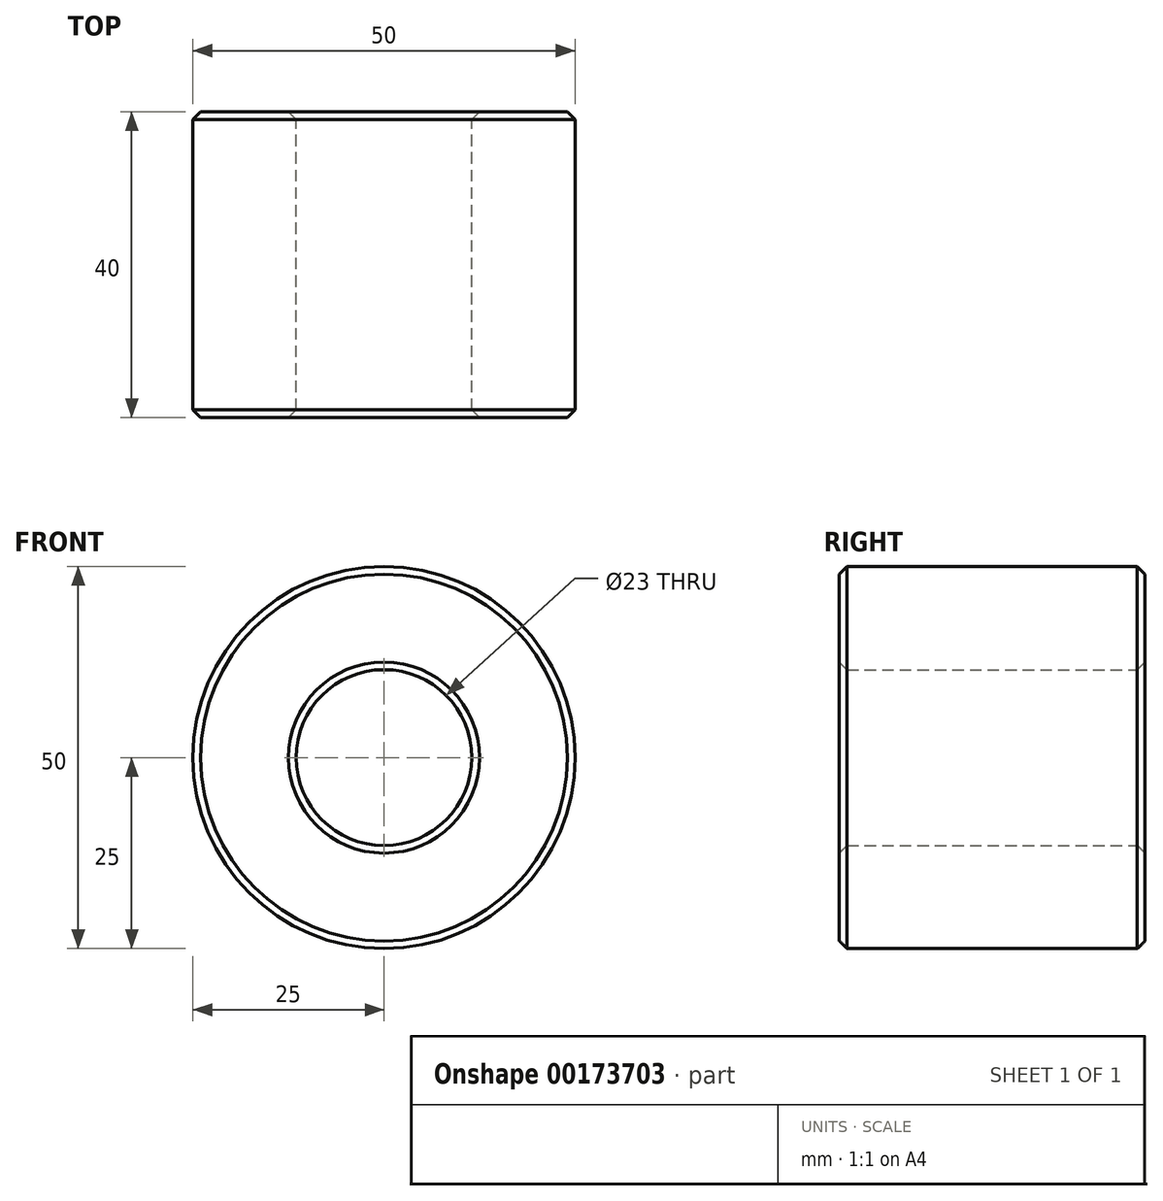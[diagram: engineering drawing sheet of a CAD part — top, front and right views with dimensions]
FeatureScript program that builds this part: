
annotation { "Feature Type Name" : "Feature", "Feature Type Description" : "" }
export const myFeature = defineFeature(function(context is Context, id is Id, definition is map)
    precondition{}
    {
        {
            var Q0;
            Q0=qCreatedBy(makeId("Front.planeOp"),FACE);
            var sketch = newSketch(context, id + "F0", { "sketchPlane" : qUnion([Q0])});
            skCircle(sketch, "E0", {"center": v(0, 0) * mm, "radius": 25 * mm});
            skCircle(sketch, "E1", {"center": v(0, 0) * mm, "radius": 11.5 * mm});
            skSolve(sketch);
        }
        {
            var Q0;
            Q0=qSketchRegion(id+"F0",true);
            extrude(context, id + "F1", {"entities" : qUnion([Q0]), "endBound" : BoundingType.SYMMETRIC, "depth" : 40 * mm});
        }
        {
            var Q0;
            Q0=makeQuery(id+"F1.opExtrude","CAP_FACE",FACE,{"disambiguationData":[OSD([sQuery(id+"F0.wireOp",EDGE,"E0"),sQuery(id+"F0.wireOp",EDGE,"E1")])],"isStart":false});
            var Q1;
            Q1=makeQuery(id+"F1.opExtrude","CAP_FACE",FACE,{"disambiguationData":[OSD([sQuery(id+"F0.wireOp",EDGE,"E0"),sQuery(id+"F0.wireOp",EDGE,"E1")])],"isStart":true});
            chamfer(context, id + "F2", {"entities" : qUnion([Q0, Q1]), "width" : 1 * mm, "tangentPropagation" : true});
        }
    });
